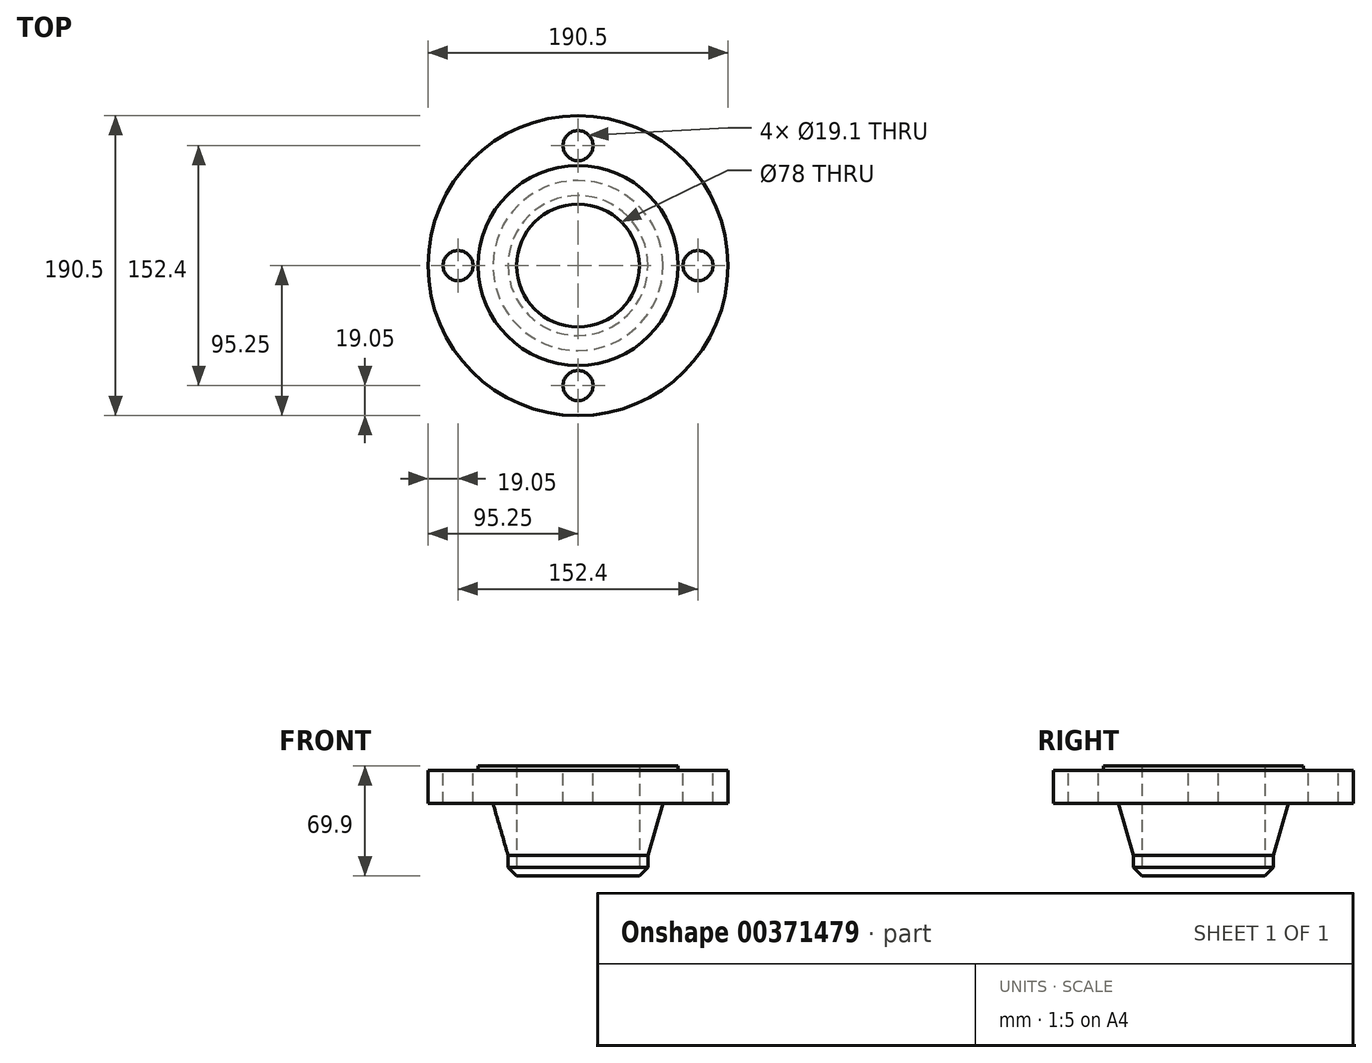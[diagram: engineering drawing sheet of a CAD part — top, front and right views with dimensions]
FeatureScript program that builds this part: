
annotation { "Feature Type Name" : "Feature", "Feature Type Description" : "" }
export const myFeature = defineFeature(function(context is Context, id is Id, definition is map)
    precondition{}
    {
        {
            var Q0;
            Q0=qCreatedBy(makeId("Front.planeOp"),FACE);
            var sketch = newSketch(context, id + "F0", { "sketchPlane" : qUnion([Q0])});
            skLineSegment(sketch, "E0", {"start": v(-39, 0) * mm, "end": v(-39, 69.9) * mm});
            skLineSegment(sketch, "E1", {"start": v(-39, 69.9) * mm, "end": v(-63.5, 69.9) * mm});
            skLineSegment(sketch, "E2", {"start": v(-63.5, 69.9) * mm, "end": v(-63.5, 68.9) * mm});
            skLineSegment(sketch, "E3", {"start": v(-65.5, 66.9) * mm, "end": v(-95.25, 66.9) * mm});
            skLineSegment(sketch, "E4", {"start": v(-95.25, 66.9) * mm, "end": v(-95.25, 46) * mm});
            skLineSegment(sketch, "E5", {"start": v(-95.25, 46) * mm, "end": v(-54, 46) * mm});
            skLineSegment(sketch, "E6", {"start": v(-44.45, 5.45) * mm, "end": v(-39, 0) * mm});
            skLineSegment(sketch, "E7", {"start": v(-44.45, 5.45) * mm, "end": v(-44.45, 13.16) * mm});
            skLineSegment(sketch, "E8", {"start": v(-44.45, 13.16) * mm, "end": v(-54, 46) * mm});
            skPoint(sketch, "E9.visualSharp", {"position": v(-63.5, 66.9) * mm});
            skArc(sketch, "E9.filletArc", {"start": v(-65.5, 66.9) * mm, "mid": v(-64.09, 67.49) * mm, "end": v(-63.5, 68.9) * mm});
            skLineSegment(sketch, "E10", {"start": v(0, 0) * mm, "end": v(0, 72.12) * mm, "construction": true});
            skSolve(sketch);
        }
        {
            var Q0;
            Q0=qSketchRegion(id+"F0",true);
            var Q1;
            Q1=sQuery(id+"F0.wireOp",EDGE,"E10");
            revolve(context, id + "F1", {"entities" : qUnion([Q0]), "axis" : qUnion([Q1]), "revolveType" : RevolveType.FULL});
        }
        {
            var Q0;
            Q0=makeQuery(id+"F1.opRevolve","SWEPT_FACE",FACE,{"disambiguationData":[OSD([sQuery(id+"F0.wireOp",EDGE,"E3")])]});
            var sketch = newSketch(context, id + "F2", { "sketchPlane" : qUnion([Q0])});
            skCircle(sketch, "E11", {"center": v(0, 0) * mm, "radius": 76.2 * mm, "construction": true});
            skCircle(sketch, "E12", {"center": v(0, 76.2) * mm, "radius": 9.55 * mm});
            skCircle(sketch, "E13.1.0", {"center": v(-76.2, 0) * mm, "radius": 9.55 * mm});
            skCircle(sketch, "E13.2.0", {"center": v(0, -76.2) * mm, "radius": 9.55 * mm});
            skCircle(sketch, "E13.3.0", {"center": v(76.2, 0) * mm, "radius": 9.55 * mm});
            skSolve(sketch);
        }
        {
            var Q0;
            Q0=makeQuery(id+"F2.imprint","IMPRINT",FACE,{"disambiguationData":[TD([[makeQuery(id+"F2.imprint","IMPRINT",EDGE,{"derivedFrom":sQuery(id+"F2.wireOp",EDGE,"E13.1.0")}),1.0]])]});
            var Q1;
            Q1=makeQuery(id+"F2.imprint","IMPRINT",FACE,{"disambiguationData":[TD([[makeQuery(id+"F2.imprint","IMPRINT",EDGE,{"derivedFrom":sQuery(id+"F2.wireOp",EDGE,"E13.2.0")}),1.0]])]});
            var Q2;
            Q2=makeQuery(id+"F2.imprint","IMPRINT",FACE,{"disambiguationData":[TD([[makeQuery(id+"F2.imprint","IMPRINT",EDGE,{"derivedFrom":sQuery(id+"F2.wireOp",EDGE,"E13.3.0")}),1.0]])]});
            var Q3;
            Q3=makeQuery(id+"F2.imprint","IMPRINT",FACE,{"disambiguationData":[TD([[makeQuery(id+"F2.imprint","IMPRINT",EDGE,{"derivedFrom":sQuery(id+"F2.wireOp",EDGE,"E12")}),1.0]])]});
            extrude(context, id + "F3", {"entities" : qUnion([Q0, Q1, Q2, Q3]), "operationType" : NewBodyOperationType.REMOVE, "endBound" : BoundingType.THROUGH_ALL, "oppositeDirection" : true, "depth" : 25.4 * mm});
        }
    });
